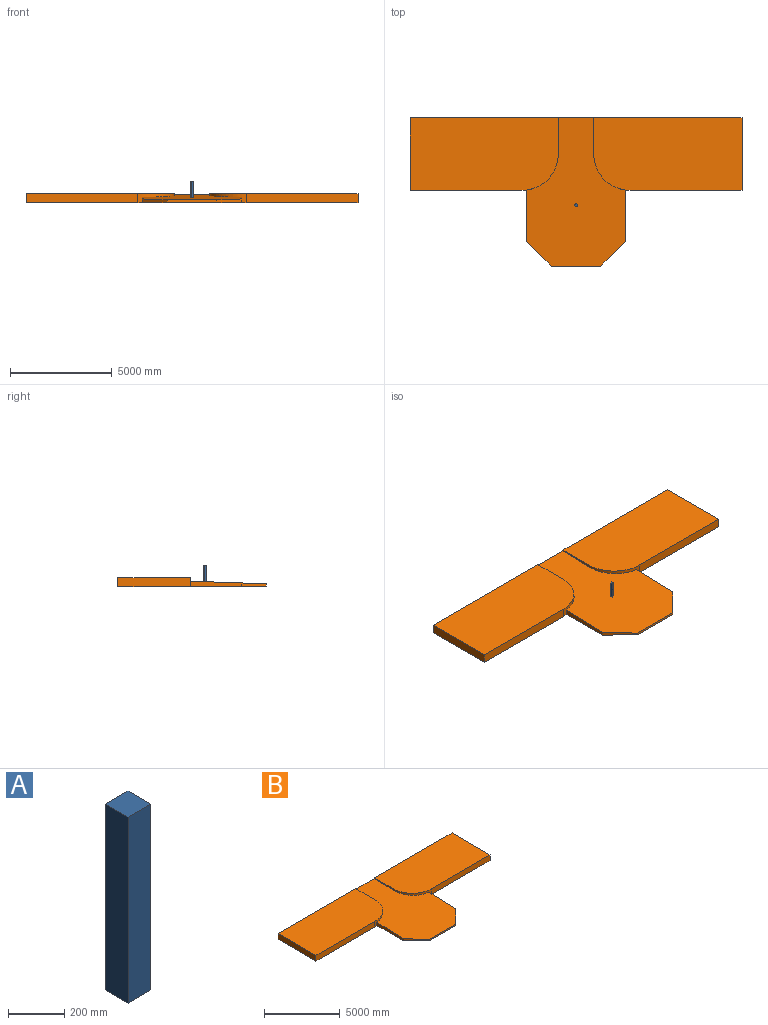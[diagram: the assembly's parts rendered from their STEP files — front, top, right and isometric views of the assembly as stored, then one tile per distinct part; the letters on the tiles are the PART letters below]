
ASSEMBLY  parts=2 mates=1
PART A: 6 faces, bbox 114.3x114.3x812.8 mm
  f0: plane 812.8x114.3mm, normal (1,0,0), area 92903mm2, adj f1,f3,f4,f5
  f1: plane 812.8x114.3mm, normal (0,1,0), area 92903mm2, adj f0,f2,f4,f5
  f2: plane 812.8x114.3mm, normal (-1,0,0), area 92903mm2, adj f1,f3,f4,f5
  f3: plane 812.8x114.3mm, normal (0,-1,0), area 92903mm2, adj f0,f2,f4,f5
  f4: plane 114.3x114.3mm, normal (0,0,1), area 13064.5mm2, adj f0,f1,f2,f3
  f5: plane 114.3x114.3mm, normal (0,0,-1), area 13064.5mm2, adj f0,f1,f2,f3
PART B: 24 faces, bbox 16299.4x7275.4x457.2 mm
  f0: plane 2513.01x261.06mm, normal (1,0,0), area 526411.1mm2, adj f1,f3,f7,f23
  f1: plane 7274.74x4876.8mm, normal (0,-0.03,1), area 24229685.3mm2, adj f0,f2,f4,f5,f6,f7,f14,f15
  f2: plane 2438.4x107.95mm, normal (0,-1,0.01), area 263225.3mm2, adj f1,f3,f22,f23
  f3: plane 7275.4x4876.8mm, normal (0,-0.01,-1), area 24218966.6mm2, adj f0,f2,f4,f5,f7,f8,f15,f17
  f4: plane 4876.8x406.44mm, normal (0,1,0), area 1982128.4mm2, adj f1,f3,f11,f13,f16,f21
  f5: plane 2513.01x261.06mm, normal (-1,0,0), area 526411.1mm2, adj f1,f3,f15,f22
  f6: plane 1778x112.85mm, normal (-1,0,0), area 145447.8mm2, adj f1,f7,f11,f12
  f7: cylinder r=1778mm len=1778mm, axis (0,0,-1), area 530871.8mm2, adj f0,f1,f3,f6,f8,f9,f12,f13
  f8: plane 1778x10.86mm, normal (-1,0,0), area 9658mm2, adj f3,f7,f13
  f9: plane 5498.39x457.2mm, normal (0,-1,0), area 2513862.1mm2, adj f7,f10,f12,f13
  f10: plane 3556x457.2mm, normal (1,0,0), area 1625803.2mm2, adj f9,f11,f12,f13
  f11: plane 7276.39x457.2mm, normal (0,1,0), area 2690658.7mm2, adj f4,f6,f10,f12,f13
  f12: plane 7276.39x3556mm, normal (0,0,1), area 25196411.4mm2, adj f6,f7,f9,f10,f11
  f13: plane 7276.39x3556mm, normal (0,0,-1), area 25196411.4mm2, adj f4,f7,f8,f9,f10,f11
  f14: plane 1778x112.85mm, normal (1,0,0), area 145447.8mm2, adj f1,f15,f16,f20
  f15: cylinder r=1778mm len=1778mm, axis (0,0,-1), area 530871.8mm2, adj f1,f3,f5,f14,f17,f19,f20,f21
  f16: plane 7276.39x457.2mm, normal (0,1,0), area 2690658.7mm2, adj f4,f14,f18,f20,f21
  f17: plane 1778x10.86mm, normal (1,0,0), area 9658mm2, adj f3,f15,f21
  f18: plane 3556x457.2mm, normal (-1,0,0), area 1625803.2mm2, adj f16,f19,f20,f21
  f19: plane 5498.39x457.2mm, normal (0,-1,0), area 2513862.1mm2, adj f15,f18,f20,f21
  f20: plane 7276.39x3556mm, normal (0,0,1), area 25196411.4mm2, adj f14,f15,f16,f18,f19
  f21: plane 7276.39x3556mm, normal (0,0,-1), area 25196411.2mm2, adj f4,f15,f16,f17,f18,f19
  f22: plane 1220.14x1219.2mm, normal (-0.71,-0.71,0), area 229264.2mm2, adj f1,f2,f3,f5
  f23: plane 1220.14x1219.2mm, normal (0.71,-0.71,0), area 229264.2mm2, adj f0,f1,f2,f3
PLACE A rot(axis=(0.01,-0.02,1),108deg) t=(10.01,-1551.18,833.74)mm
PLACE B t=(10.01,915.24,-236)mm fixed
MATE revolute A.f5 <-> B.f1  axis (0,0.03,-1) through (10.01,-1522.82,21.44)mm
